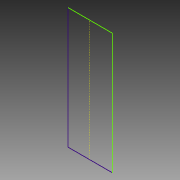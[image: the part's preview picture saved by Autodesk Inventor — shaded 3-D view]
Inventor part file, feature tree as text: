
AUTODESK INVENTOR PART (.ipt)
format: ipt  version: 2013 (Build 170138000, 138)  size: 60,928 bytes
history: native  units: in
note: dims shown in document units (in); Inventor stores cm internally (conversion verified against a paired STEP export)
features: sketch x1
ambient origin geometry x8: Origin, YZ Plane, XZ Plane, XY Plane, X Axis, Y Axis, Z Axis, Center Point
feature tree (1):
  sketch  "Sketch1"
